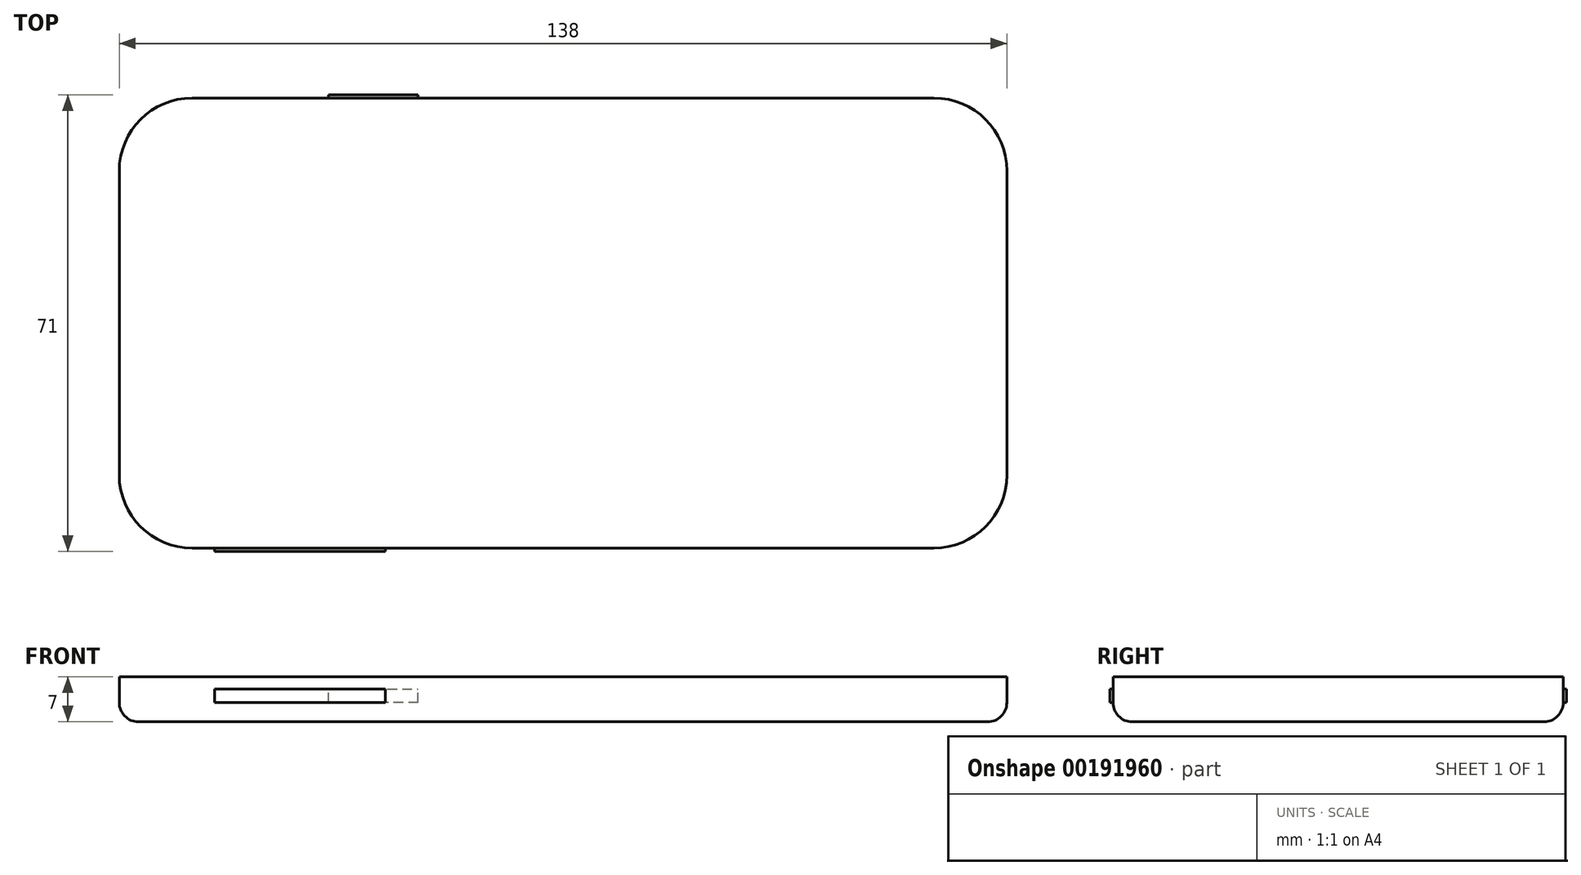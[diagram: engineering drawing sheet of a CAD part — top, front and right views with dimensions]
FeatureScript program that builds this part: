
annotation { "Feature Type Name" : "Feature", "Feature Type Description" : "" }
export const myFeature = defineFeature(function(context is Context, id is Id, definition is map)
    precondition{}
    {
        {
            var Q0;
            Q0=qCreatedBy(makeId("Top.planeOp"),FACE);
            var sketch = newSketch(context, id + "F0", { "sketchPlane" : qUnion([Q0])});
            skLineSegment(sketch, "E0.bottom", {"start": v(69, -35) * mm, "end": v(-69, -35) * mm});
            skLineSegment(sketch, "E0.top", {"start": v(69, 35) * mm, "end": v(-69, 35) * mm});
            skLineSegment(sketch, "E0.left", {"start": v(69, -35) * mm, "end": v(69, 35) * mm});
            skLineSegment(sketch, "E0.right", {"start": v(-69, -35) * mm, "end": v(-69, 35) * mm});
            skPoint(sketch, "E0.middle", {"position": v(0, 0) * mm});
            skSolve(sketch);
        }
        {
            var Q0;
            Q0=makeQuery(id+"F0.imprint","IMPRINT",FACE,{"disambiguationData":[TD([[makeQuery(id+"F0.imprint","IMPRINT",EDGE,{"derivedFrom":sQuery(id+"F0.wireOp",EDGE,"E0.bottom")}),-1.0]])]});
            extrude(context, id + "F1", {"entities" : qUnion([Q0]), "depth" : 7 * mm});
        }
        {
            var Q0;
            Q0=makeQuery(id+"F1.opExtrude","SWEPT_EDGE",EDGE,{"disambiguationData":[OSD([sQuery(id+"F0.wireOp",EDGE,"E0.bottom"),sQuery(id+"F0.wireOp",EDGE,"E0.left")])]});
            var Q1;
            Q1=makeQuery(id+"F1.opExtrude","SWEPT_EDGE",EDGE,{"disambiguationData":[OSD([sQuery(id+"F0.wireOp",EDGE,"E0.top"),sQuery(id+"F0.wireOp",EDGE,"E0.left")])]});
            var Q2;
            Q2=makeQuery(id+"F1.opExtrude","SWEPT_EDGE",EDGE,{"disambiguationData":[OSD([sQuery(id+"F0.wireOp",EDGE,"E0.bottom"),sQuery(id+"F0.wireOp",EDGE,"E0.right")])]});
            var Q3;
            Q3=makeQuery(id+"F1.opExtrude","SWEPT_EDGE",EDGE,{"disambiguationData":[OSD([sQuery(id+"F0.wireOp",EDGE,"E0.top"),sQuery(id+"F0.wireOp",EDGE,"E0.right")])]});
            fillet(context, id + "F2", {"entities" : qUnion([Q0, Q1, Q2, Q3]), "radius" : 11.35 * mm, "tangentPropagation" : true, "allowEdgeOverflow" : false});
        }
        {
            var Q0;
            Q0=makeQuery(id+"F1.opExtrude","CAP_EDGE",EDGE,{"disambiguationData":[OSD([sQuery(id+"F0.wireOp",EDGE,"E0.top")])],"isStart":true});
            var Q1;
            Q1=makeQuery(id+"F1.opExtrude","CAP_EDGE",EDGE,{"disambiguationData":[OSD([sQuery(id+"F0.wireOp",EDGE,"E0.bottom")])],"isStart":true});
            var Q2;
            Q2=makeQuery(id+"F1.opExtrude","CAP_EDGE",EDGE,{"disambiguationData":[OSD([sQuery(id+"F0.wireOp",EDGE,"E0.right")])],"isStart":true});
            var Q3;
            Q3=makeQuery(id+"F1.opExtrude","CAP_EDGE",EDGE,{"disambiguationData":[OSD([sQuery(id+"F0.wireOp",EDGE,"E0.left")])],"isStart":true});
            fillet(context, id + "F3", {"entities" : qUnion([Q0, Q1, Q2, Q3]), "radius" : 3 * mm, "tangentPropagation" : true, "allowEdgeOverflow" : false});
        }
        {
            var Q0;
            Q0=makeQuery(id+"F1.opExtrude","SWEPT_FACE",FACE,{"disambiguationData":[OSD([sQuery(id+"F0.wireOp",EDGE,"E0.bottom")])]});
            var sketch = newSketch(context, id + "F4", { "sketchPlane" : qUnion([Q0])});
            skLineSegment(sketch, "E1.bottom", {"start": v(-54.2, 5.07) * mm, "end": v(-27.63, 5.07) * mm});
            skLineSegment(sketch, "E1.top", {"start": v(-54.2, 3) * mm, "end": v(-27.63, 3) * mm});
            skLineSegment(sketch, "E1.left", {"start": v(-54.2, 5.07) * mm, "end": v(-54.2, 3) * mm});
            skLineSegment(sketch, "E1.right", {"start": v(-27.63, 5.07) * mm, "end": v(-27.63, 3) * mm});
            skSolve(sketch);
        }
        {
            var Q0;
            Q0=makeQuery(id+"F4.imprint","IMPRINT",FACE,{"disambiguationData":[TD([[makeQuery(id+"F4.imprint","IMPRINT",EDGE,{"derivedFrom":sQuery(id+"F4.wireOp",EDGE,"E1.bottom")}),-1.0]])]});
            extrude(context, id + "F5", {"entities" : qUnion([Q0]), "operationType" : NewBodyOperationType.ADD, "depth" : .5 * mm});
        }
        {
            var Q0;
            Q0=makeQuery(id+"F1.opExtrude","SWEPT_FACE",FACE,{"disambiguationData":[OSD([sQuery(id+"F0.wireOp",EDGE,"E0.top")])]});
            var sketch = newSketch(context, id + "F6", { "sketchPlane" : qUnion([Q0])});
            skLineSegment(sketch, "E2.bottom", {"start": v(36.49, 3) * mm, "end": v(22.54, 3) * mm});
            skLineSegment(sketch, "E2.top", {"start": v(36.49, 5.11) * mm, "end": v(22.54, 5.11) * mm});
            skLineSegment(sketch, "E2.left", {"start": v(36.49, 3) * mm, "end": v(36.49, 5.11) * mm});
            skLineSegment(sketch, "E2.right", {"start": v(22.54, 3) * mm, "end": v(22.54, 5.11) * mm});
            skSolve(sketch);
        }
        {
            var Q0;
            Q0=makeQuery(id+"F6.imprint","IMPRINT",FACE,{"disambiguationData":[TD([[makeQuery(id+"F6.imprint","IMPRINT",EDGE,{"derivedFrom":sQuery(id+"F6.wireOp",EDGE,"E2.bottom")}),1.0]])]});
            extrude(context, id + "F7", {"entities" : qUnion([Q0]), "operationType" : NewBodyOperationType.ADD, "depth" : .5 * mm});
        }
    });
